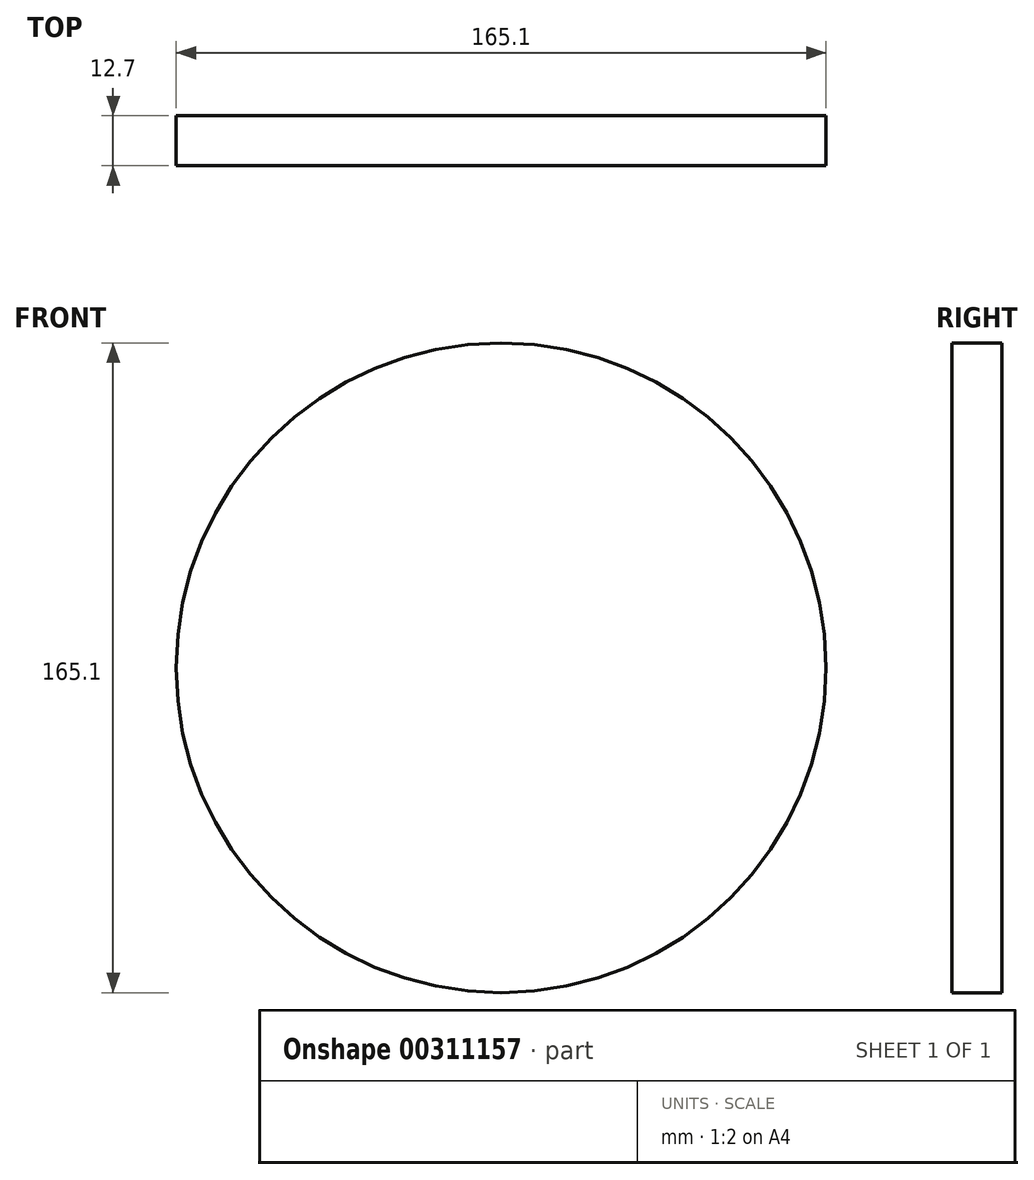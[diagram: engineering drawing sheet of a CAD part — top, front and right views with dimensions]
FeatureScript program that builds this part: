
annotation { "Feature Type Name" : "Feature", "Feature Type Description" : "" }
export const myFeature = defineFeature(function(context is Context, id is Id, definition is map)
    precondition{}
    {
        {
            var Q0;
            Q0=qCreatedBy(makeId("Front.planeOp"),FACE);
            var sketch = newSketch(context, id + "F0", { "sketchPlane" : qUnion([Q0])});
            skCircle(sketch, "E0", {"center": v(0, 0) * mm, "radius": 82.55 * mm});
            skSolve(sketch);
        }
        {
            var Q0;
            Q0=makeQuery(id+"F0.imprint","IMPRINT",FACE,{"disambiguationData":[TD([[makeQuery(id+"F0.imprint","IMPRINT",EDGE,{"derivedFrom":sQuery(id+"F0.wireOp",EDGE,"E0")}),1.0]])]});
            extrude(context, id + "F1", {"entities" : qUnion([Q0]), "depth" : 12.7 * mm});
        }
    });
